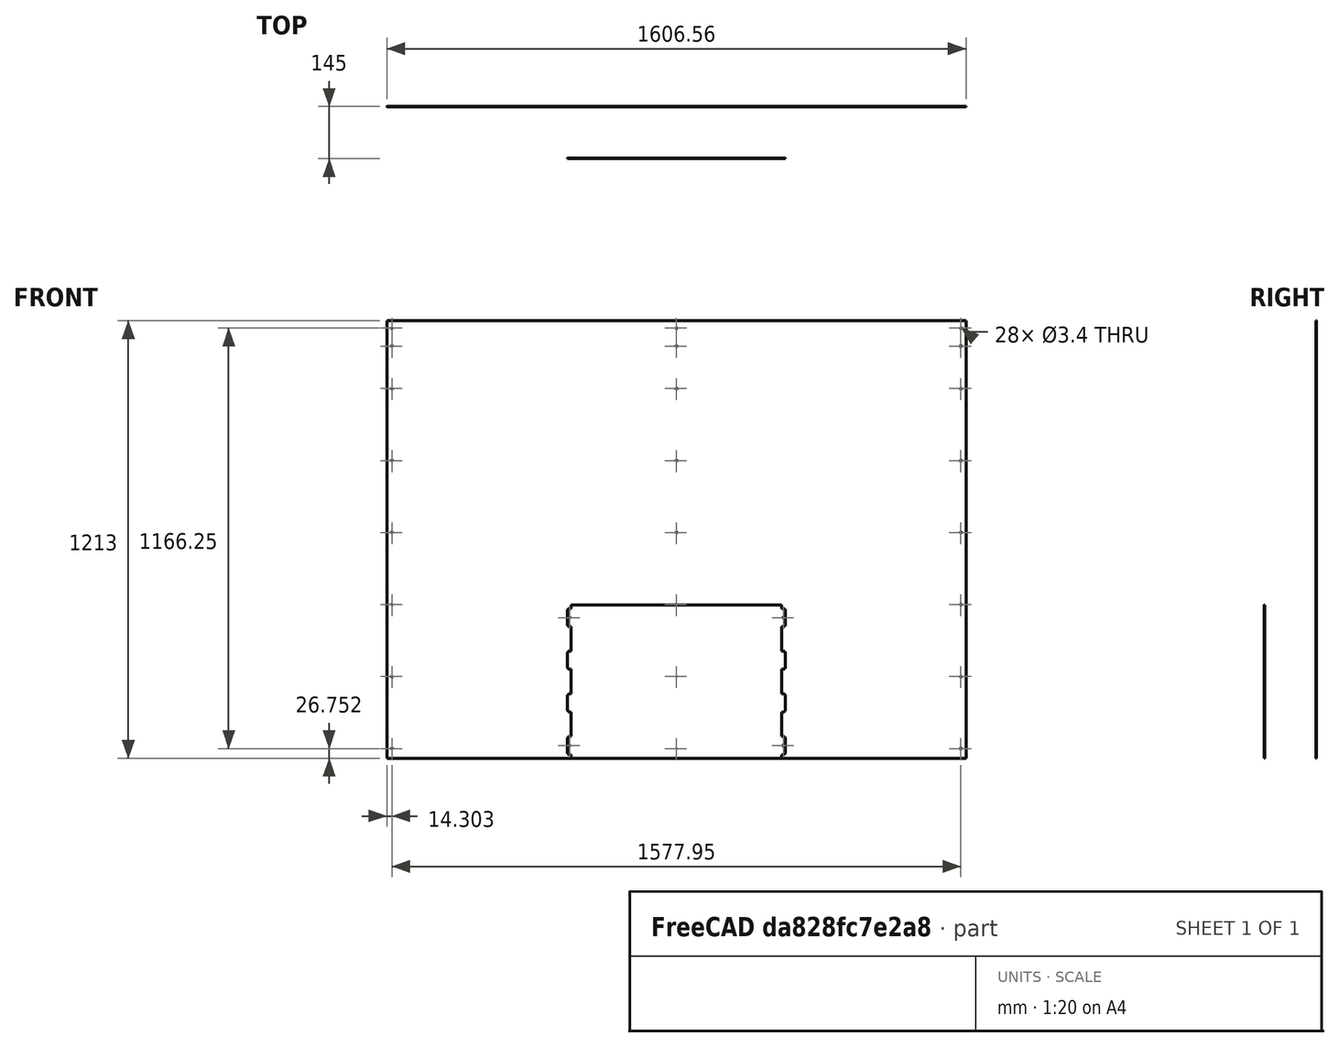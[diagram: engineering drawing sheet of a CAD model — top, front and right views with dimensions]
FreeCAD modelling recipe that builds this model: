
FCSTD DOCUMENT  (FreeCAD 0.21R32532 (Git))
Label: composit_full_size2part_plexiglass_cut
License: All rights reserved
LicenseURL: http://en.wikipedia.org/wiki/All_rights_reserved
objects: Sketcher::SketchObject×8, App::Link×3, Part::Feature×2, Part::FeaturePython×2, Part::Part2DObjectPython×1
note: 11 computed .brp shape members not serialized (recipe doc carries the construction recipe); baked Part::Feature solids carry a one-line shape summary decoded from their .brp
EXTERNAL_REF file=composit_full_size2part.FCStd obj=plexiglasss_shield
EXTERNAL_REF file=composit_full_size2part.FCStd obj=Body048
EXTERNAL_REF file=composit_full_size2part.FCStd obj=Body057

FEATURE [App::Link] Link
  LinkedObject = -> <external composit_full_size2part.FCStd>#plexiglasss_shield
  expr: LinkedObject = composit_full_size2part#plexiglasss_shield._self
FEATURE [App::Link] Link001
  LinkedObject = -> <external composit_full_size2part.FCStd>#Body048
  expr: LinkedObject = composit_full_size2part#<<plexiglass_shield_material_0.30ansi>>._self
FEATURE [Part::Feature] Unfold
  shape: bbox 1607 x 1 x 1213 mm, 30 faces (baked)
FEATURE [Sketcher::SketchObject] Unfold_Sketch
  FullyConstrained = false
  sketch-geometry (28):
    g0: LineSegment StartX=-803.277 StartY=0 StartZ=0 EndX=-803.277 EndY=-1213 EndZ=0
    g1: LineSegment StartX=803.277 StartY=0 StartZ=0 EndX=803.277 EndY=-1213 EndZ=0
    g2: Circle CenterX=788.977 CenterY=-1193 CenterZ=0 NormalX=0 NormalY=0 NormalZ=-1 AngleXU=-3.14159 Radius=1.7
    g3: Circle CenterX=788.977 CenterY=-1143.07 CenterZ=0 NormalX=0 NormalY=0 NormalZ=-1 AngleXU=-3.14159 Radius=1.7
    g4: Circle CenterX=788.977 CenterY=-1025.25 CenterZ=0 NormalX=0 NormalY=0 NormalZ=-1 AngleXU=-3.14159 Radius=1.7
    g5: Circle CenterX=-788.977 CenterY=-625.852 CenterZ=0 NormalX=0 NormalY=0 NormalZ=-1 AngleXU=-3.14159 Radius=1.7
    g6: Circle CenterX=-788.977 CenterY=-825.552 CenterZ=0 NormalX=0 NormalY=0 NormalZ=-1 AngleXU=-3.14159 Radius=1.7
    g7: Circle CenterX=-788.977 CenterY=-1025.25 CenterZ=0 NormalX=0 NormalY=0 NormalZ=-1 AngleXU=-3.14159 Radius=1.7
    g8: Circle CenterX=-788.977 CenterY=-1143.07 CenterZ=0 NormalX=0 NormalY=0 NormalZ=-1 AngleXU=-3.14159 Radius=1.7
    g9: Circle CenterX=-788.977 CenterY=-1193 CenterZ=0 NormalX=0 NormalY=0 NormalZ=-1 AngleXU=-3.14159 Radius=1.7
    g10: Circle CenterX=788.977 CenterY=-825.552 CenterZ=0 NormalX=0 NormalY=0 NormalZ=-1 AngleXU=-3.14159 Radius=1.7
    g11: Circle CenterX=788.977 CenterY=-625.852 CenterZ=0 NormalX=0 NormalY=0 NormalZ=-1 AngleXU=-3.14159 Radius=1.7
    g12: Circle CenterX=-7.45e-13 CenterY=-625.852 CenterZ=0 NormalX=0 NormalY=0 NormalZ=-1 AngleXU=-3.14159 Radius=1.7
    g13: Circle CenterX=-7.45e-13 CenterY=-1193 CenterZ=0 NormalX=0 NormalY=0 NormalZ=-1 AngleXU=-3.14159 Radius=1.7
    g14: Circle CenterX=-7.45e-13 CenterY=-1143.07 CenterZ=0 NormalX=0 NormalY=0 NormalZ=-1 AngleXU=-3.14159 Radius=1.7
    g15: Circle CenterX=-7.45e-13 CenterY=-1025.25 CenterZ=0 NormalX=0 NormalY=0 NormalZ=-1 AngleXU=-3.14159 Radius=1.7
    g16: Circle CenterX=-7.45e-13 CenterY=-825.552 CenterZ=0 NormalX=0 NormalY=0 NormalZ=-1 AngleXU=-3.14159 Radius=1.7
    g17: Circle CenterX=788.977 CenterY=-26.752 CenterZ=0 NormalX=0 NormalY=0 NormalZ=-1 AngleXU=-3.14159 Radius=1.7
    g18: Circle CenterX=-788.977 CenterY=-26.752 CenterZ=0 NormalX=0 NormalY=0 NormalZ=-1 AngleXU=-3.14159 Radius=1.7
    g19: Circle CenterX=788.977 CenterY=-226.452 CenterZ=0 NormalX=0 NormalY=0 NormalZ=-1 AngleXU=-3.14159 Radius=1.7
    g20: Circle CenterX=788.977 CenterY=-426.152 CenterZ=0 NormalX=0 NormalY=0 NormalZ=-1 AngleXU=-3.14159 Radius=1.7
    g21: Circle CenterX=-788.977 CenterY=-426.152 CenterZ=0 NormalX=0 NormalY=0 NormalZ=-1 AngleXU=-3.14159 Radius=1.7
    g22: Circle CenterX=-788.977 CenterY=-226.452 CenterZ=0 NormalX=0 NormalY=0 NormalZ=-1 AngleXU=-3.14159 Radius=1.7
    g23: Circle CenterX=-7.45e-13 CenterY=-26.752 CenterZ=0 NormalX=0 NormalY=0 NormalZ=-1 AngleXU=-3.14159 Radius=1.7
    g24: Circle CenterX=-7.45e-13 CenterY=-426.152 CenterZ=0 NormalX=0 NormalY=0 NormalZ=-1 AngleXU=-3.14159 Radius=1.7
    g25: Circle CenterX=-7.45e-13 CenterY=-226.452 CenterZ=0 NormalX=0 NormalY=0 NormalZ=-1 AngleXU=-3.14159 Radius=1.7
    g26: LineSegment StartX=-803.277 StartY=-1213 StartZ=0 EndX=803.277 EndY=-1213 EndZ=0
    g27: LineSegment StartX=803.277 StartY=0 StartZ=0 EndX=-803.277 EndY=0 EndZ=0
FEATURE [Sketcher::SketchObject] Unfold_Sketch_Outline
  FullyConstrained = false
  sketch-geometry (4):
    g0: LineSegment StartX=803.277 StartY=0 StartZ=0 EndX=-803.277 EndY=0 EndZ=0
    g1: LineSegment StartX=-803.277 StartY=0 StartZ=0 EndX=-803.277 EndY=-1213 EndZ=0
    g2: LineSegment StartX=-803.277 StartY=-1213 StartZ=0 EndX=803.277 EndY=-1213 EndZ=0
    g3: LineSegment StartX=803.277 StartY=0 StartZ=0 EndX=803.277 EndY=-1213 EndZ=0
FEATURE [Sketcher::SketchObject] Unfold_Sketch_Internal
  FullyConstrained = false
  sketch-geometry (24):
    g0: Circle CenterX=-7.45e-13 CenterY=-226.452 CenterZ=0 NormalX=0 NormalY=0 NormalZ=-1 AngleXU=-3.14159 Radius=1.7
    g1: Circle CenterX=-7.45e-13 CenterY=-426.152 CenterZ=0 NormalX=0 NormalY=0 NormalZ=-1 AngleXU=-3.14159 Radius=1.7
    g2: Circle CenterX=-7.45e-13 CenterY=-825.552 CenterZ=0 NormalX=0 NormalY=0 NormalZ=-1 AngleXU=-3.14159 Radius=1.7
    g3: Circle CenterX=-7.45e-13 CenterY=-1025.25 CenterZ=0 NormalX=0 NormalY=0 NormalZ=-1 AngleXU=-3.14159 Radius=1.7
    g4: Circle CenterX=-7.45e-13 CenterY=-1143.07 CenterZ=0 NormalX=0 NormalY=0 NormalZ=-1 AngleXU=-3.14159 Radius=1.7
    g5: Circle CenterX=-7.45e-13 CenterY=-1193 CenterZ=0 NormalX=0 NormalY=0 NormalZ=-1 AngleXU=-3.14159 Radius=1.7
    g6: Circle CenterX=-7.45e-13 CenterY=-625.852 CenterZ=0 NormalX=0 NormalY=0 NormalZ=-1 AngleXU=-3.14159 Radius=1.7
    g7: Circle CenterX=-7.45e-13 CenterY=-26.752 CenterZ=0 NormalX=0 NormalY=0 NormalZ=-1 AngleXU=-3.14159 Radius=1.7
    g8: Circle CenterX=-788.977 CenterY=-226.452 CenterZ=0 NormalX=0 NormalY=0 NormalZ=-1 AngleXU=-3.14159 Radius=1.7
    g9: Circle CenterX=-788.977 CenterY=-426.152 CenterZ=0 NormalX=0 NormalY=0 NormalZ=-1 AngleXU=-3.14159 Radius=1.7
    g10: Circle CenterX=788.977 CenterY=-426.152 CenterZ=0 NormalX=0 NormalY=0 NormalZ=-1 AngleXU=-3.14159 Radius=1.7
    g11: Circle CenterX=788.977 CenterY=-226.452 CenterZ=0 NormalX=0 NormalY=0 NormalZ=-1 AngleXU=-3.14159 Radius=1.7
    g12: Circle CenterX=788.977 CenterY=-625.852 CenterZ=0 NormalX=0 NormalY=0 NormalZ=-1 AngleXU=-3.14159 Radius=1.7
    g13: Circle CenterX=788.977 CenterY=-825.552 CenterZ=0 NormalX=0 NormalY=0 NormalZ=-1 AngleXU=-3.14159 Radius=1.7
    g14: Circle CenterX=-788.977 CenterY=-1193 CenterZ=0 NormalX=0 NormalY=0 NormalZ=-1 AngleXU=-3.14159 Radius=1.7
    g15: Circle CenterX=-788.977 CenterY=-1143.07 CenterZ=0 NormalX=0 NormalY=0 NormalZ=-1 AngleXU=-3.14159 Radius=1.7
    g16: Circle CenterX=-788.977 CenterY=-1025.25 CenterZ=0 NormalX=0 NormalY=0 NormalZ=-1 AngleXU=-3.14159 Radius=1.7
    g17: Circle CenterX=-788.977 CenterY=-825.552 CenterZ=0 NormalX=0 NormalY=0 NormalZ=-1 AngleXU=-3.14159 Radius=1.7
    g18: Circle CenterX=-788.977 CenterY=-625.852 CenterZ=0 NormalX=0 NormalY=0 NormalZ=-1 AngleXU=-3.14159 Radius=1.7
    g19: Circle CenterX=788.977 CenterY=-1025.25 CenterZ=0 NormalX=0 NormalY=0 NormalZ=-1 AngleXU=-3.14159 Radius=1.7
    g20: Circle CenterX=788.977 CenterY=-1143.07 CenterZ=0 NormalX=0 NormalY=0 NormalZ=-1 AngleXU=-3.14159 Radius=1.7
    g21: Circle CenterX=788.977 CenterY=-1193 CenterZ=0 NormalX=0 NormalY=0 NormalZ=-1 AngleXU=-3.14159 Radius=1.7
    g22: Circle CenterX=-788.977 CenterY=-26.752 CenterZ=0 NormalX=0 NormalY=0 NormalZ=-1 AngleXU=-3.14159 Radius=1.7
    g23: Circle CenterX=788.977 CenterY=-26.752 CenterZ=0 NormalX=0 NormalY=0 NormalZ=-1 AngleXU=-3.14159 Radius=1.7
FEATURE [Sketcher::SketchObject] Unfold_Sketch_bends
  FullyConstrained = false
  sketch-geometry (6):
    g0: LineSegment StartX=-678.962 StartY=-1213 StartZ=0 EndX=-678.962 EndY=0 EndZ=0
    g1: LineSegment StartX=-394.489 StartY=-1213 StartZ=0 EndX=-394.489 EndY=0 EndZ=0
    g2: LineSegment StartX=-110.015 StartY=-1213 StartZ=0 EndX=-110.015 EndY=0 EndZ=0
    g3: LineSegment StartX=678.962 StartY=-1213 StartZ=0 EndX=678.962 EndY=0 EndZ=0
    g4: LineSegment StartX=394.489 StartY=-1213 StartZ=0 EndX=394.489 EndY=0 EndZ=0
    g5: LineSegment StartX=110.015 StartY=-1213 StartZ=0 EndX=110.015 EndY=0 EndZ=0
FEATURE [Part::Feature] Unfold001
  shape: bbox 603.8 x 1.5 x 425 mm, 58 faces (baked)
FEATURE [Sketcher::SketchObject] Unfold_Sketch001
  FullyConstrained = false
  sketch-geometry (56):
    g0: LineSegment StartX=0 StartY=291.917 StartZ=0 EndX=-10 EndY=291.917 EndZ=0
    g1: LineSegment StartX=-10 StartY=291.917 StartZ=0 EndX=-10 EndY=296.917 EndZ=0
    g2: ArcOfCircle CenterX=-15 CenterY=296.917 CenterZ=0 NormalX=0 NormalY=0 NormalZ=1 AngleXU=1.5708 Radius=5 StartAngle=4.71239 EndAngle=6.28319
    g3: LineSegment StartX=-15 StartY=301.917 StartZ=0 EndX=-55 EndY=301.917 EndZ=0
    g4: ArcOfCircle CenterX=-55 CenterY=296.917 CenterZ=0 NormalX=0 NormalY=0 NormalZ=1 AngleXU=1.5708 Radius=5 StartAngle=0 EndAngle=1.5708
    g5: LineSegment StartX=-60 StartY=296.917 StartZ=0 EndX=-60 EndY=291.917 EndZ=0
    g6: LineSegment StartX=-60 StartY=291.917 StartZ=0 EndX=-128.333 EndY=291.917 EndZ=0
    g7: LineSegment StartX=-128.333 StartY=291.917 StartZ=0 EndX=-128.333 EndY=296.917 EndZ=0
    g8: ArcOfCircle CenterX=-133.333 CenterY=296.917 CenterZ=0 NormalX=0 NormalY=0 NormalZ=1 AngleXU=1.5708 Radius=5 StartAngle=4.71239 EndAngle=6.28319
    g9: LineSegment StartX=-133.333 StartY=301.917 StartZ=0 EndX=-173.333 EndY=301.917 EndZ=0
    g10: ArcOfCircle CenterX=-173.333 CenterY=296.917 CenterZ=0 NormalX=0 NormalY=0 NormalZ=1 AngleXU=1.5708 Radius=5 StartAngle=2e-15 EndAngle=1.5708
    g11: LineSegment StartX=-178.333 StartY=296.917 StartZ=0 EndX=-178.333 EndY=291.917 EndZ=0
    g12: LineSegment StartX=-178.333 StartY=291.917 StartZ=0 EndX=-246.667 EndY=291.917 EndZ=0
    g13: LineSegment StartX=-246.667 StartY=291.917 StartZ=0 EndX=-246.667 EndY=296.917 EndZ=0
    g14: ArcOfCircle CenterX=-251.667 CenterY=296.917 CenterZ=0 NormalX=0 NormalY=0 NormalZ=1 AngleXU=1.5708 Radius=5 StartAngle=4.71239 EndAngle=6.28319
    g15: LineSegment StartX=-251.667 StartY=301.917 StartZ=0 EndX=-291.667 EndY=301.917 EndZ=0
    g16: ArcOfCircle CenterX=-291.667 CenterY=296.917 CenterZ=0 NormalX=0 NormalY=0 NormalZ=1 AngleXU=1.5708 Radius=5 StartAngle=0 EndAngle=1.5708
    g17: LineSegment StartX=-296.667 StartY=296.917 StartZ=0 EndX=-296.667 EndY=291.917 EndZ=0
    g18: LineSegment StartX=-296.667 StartY=291.917 StartZ=0 EndX=-365 EndY=291.917 EndZ=0
    g19: LineSegment StartX=-365 StartY=291.917 StartZ=0 EndX=-365 EndY=296.917 EndZ=0
    g20: ArcOfCircle CenterX=-370 CenterY=296.917 CenterZ=0 NormalX=0 NormalY=0 NormalZ=1 AngleXU=1.5708 Radius=5 StartAngle=4.71239 EndAngle=6.28319
    g21: LineSegment StartX=-370 StartY=301.917 StartZ=0 EndX=-410 EndY=301.917 EndZ=0
    g22: ArcOfCircle CenterX=-410 CenterY=296.917 CenterZ=0 NormalX=0 NormalY=0 NormalZ=1 AngleXU=1.5708 Radius=5 StartAngle=0 EndAngle=1.5708
    g23: LineSegment StartX=-415 StartY=296.917 StartZ=0 EndX=-415 EndY=291.917 EndZ=0
    g24: LineSegment StartX=-415 StartY=291.917 StartZ=0 EndX=-425 EndY=291.917 EndZ=0
    g25: LineSegment StartX=0 StartY=291.917 StartZ=0 EndX=0 EndY=-291.917 EndZ=0
    g26: LineSegment StartX=-425 StartY=-291.917 StartZ=0 EndX=-425 EndY=291.917 EndZ=0
    g27: LineSegment StartX=-415 StartY=-291.917 StartZ=0 EndX=-425 EndY=-291.917 EndZ=0
    g28: LineSegment StartX=-415 StartY=-296.917 StartZ=0 EndX=-415 EndY=-291.917 EndZ=0
    g29: ArcOfCircle CenterX=-410 CenterY=-296.917 CenterZ=0 NormalX=0 NormalY=0 NormalZ=1 AngleXU=-1.5708 Radius=5 StartAngle=4.71239 EndAngle=6.28319
    g30: LineSegment StartX=-370 StartY=-301.917 StartZ=0 EndX=-410 EndY=-301.917 EndZ=0
    g31: ArcOfCircle CenterX=-370 CenterY=-296.917 CenterZ=0 NormalX=0 NormalY=0 NormalZ=1 AngleXU=-1.5708 Radius=5 StartAngle=2.7e-15 EndAngle=1.5708
    g32: LineSegment StartX=-365 StartY=-291.917 StartZ=0 EndX=-365 EndY=-296.917 EndZ=0
    g33: LineSegment StartX=-296.667 StartY=-291.917 StartZ=0 EndX=-365 EndY=-291.917 EndZ=0
    g34: LineSegment StartX=-296.667 StartY=-296.917 StartZ=0 EndX=-296.667 EndY=-291.917 EndZ=0
    g35: ArcOfCircle CenterX=-291.667 CenterY=-296.917 CenterZ=0 NormalX=0 NormalY=0 NormalZ=1 AngleXU=-1.5708 Radius=5 StartAngle=4.71239 EndAngle=6.28319
    g36: LineSegment StartX=-251.667 StartY=-301.917 StartZ=0 EndX=-291.667 EndY=-301.917 EndZ=0
    g37: ArcOfCircle CenterX=-251.667 CenterY=-296.917 CenterZ=0 NormalX=0 NormalY=0 NormalZ=1 AngleXU=-1.5708 Radius=5 StartAngle=2.7e-15 EndAngle=1.5708
    g38: LineSegment StartX=-246.667 StartY=-291.917 StartZ=0 EndX=-246.667 EndY=-296.917 EndZ=0
    g39: LineSegment StartX=-178.333 StartY=-291.917 StartZ=0 EndX=-246.667 EndY=-291.917 EndZ=0
    g40: LineSegment StartX=-178.333 StartY=-296.917 StartZ=0 EndX=-178.333 EndY=-291.917 EndZ=0
    g41: ArcOfCircle CenterX=-173.333 CenterY=-296.917 CenterZ=0 NormalX=0 NormalY=0 NormalZ=1 AngleXU=-1.5708 Radius=5 StartAngle=4.71239 EndAngle=6.28319
    g42: LineSegment StartX=-133.333 StartY=-301.917 StartZ=0 EndX=-173.333 EndY=-301.917 EndZ=0
    g43: ArcOfCircle CenterX=-133.333 CenterY=-296.917 CenterZ=0 NormalX=0 NormalY=0 NormalZ=1 AngleXU=-1.5708 Radius=5 StartAngle=0 EndAngle=1.5708
    g44: LineSegment StartX=-128.333 StartY=-291.917 StartZ=0 EndX=-128.333 EndY=-296.917 EndZ=0
    g45: LineSegment StartX=-60 StartY=-291.917 StartZ=0 EndX=-128.333 EndY=-291.917 EndZ=0
    g46: LineSegment StartX=-60 StartY=-296.917 StartZ=0 EndX=-60 EndY=-291.917 EndZ=0
    g47: ArcOfCircle CenterX=-55 CenterY=-296.917 CenterZ=0 NormalX=0 NormalY=0 NormalZ=1 AngleXU=-1.5708 Radius=5 StartAngle=4.71239 EndAngle=6.28319
    g48: LineSegment StartX=-15 StartY=-301.917 StartZ=0 EndX=-55 EndY=-301.917 EndZ=0
    g49: ArcOfCircle CenterX=-15 CenterY=-296.917 CenterZ=0 NormalX=0 NormalY=0 NormalZ=1 AngleXU=-1.5708 Radius=5 StartAngle=0 EndAngle=1.5708
    g50: LineSegment StartX=-10 StartY=-291.917 StartZ=0 EndX=-10 EndY=-296.917 EndZ=0
    g51: LineSegment StartX=0 StartY=-291.917 StartZ=0 EndX=-10 EndY=-291.917 EndZ=0
    g52: Circle CenterX=-35 CenterY=-296.417 CenterZ=0 NormalX=0 NormalY=0 NormalZ=-1 AngleXU=-1.5708 Radius=1.7
    g53: Circle CenterX=-35 CenterY=296.417 CenterZ=0 NormalX=0 NormalY=0 NormalZ=1 AngleXU=1.5708 Radius=1.7
    g54: Circle CenterX=-390 CenterY=-296.417 CenterZ=0 NormalX=0 NormalY=0 NormalZ=-1 AngleXU=-1.5708 Radius=1.7
    g55: Circle CenterX=-390 CenterY=296.417 CenterZ=0 NormalX=0 NormalY=0 NormalZ=1 AngleXU=1.5708 Radius=1.7
FEATURE [Sketcher::SketchObject] Unfold_Sketch_Outline001
  FullyConstrained = false
  Placement = pos=(302,425,0) rot=(0,0,1;1.5708rad)
  sketch-geometry (52):
    g0: LineSegment StartX=0 StartY=291.917 StartZ=0 EndX=-10 EndY=291.917 EndZ=0
    g1: LineSegment StartX=-10 StartY=291.917 StartZ=0 EndX=-10 EndY=296.917 EndZ=0
    g2: ArcOfCircle CenterX=-15 CenterY=296.917 CenterZ=0 NormalX=0 NormalY=0 NormalZ=1 AngleXU=1.5708 Radius=5 StartAngle=4.71239 EndAngle=6.28319
    g3: LineSegment StartX=-15 StartY=301.917 StartZ=0 EndX=-55 EndY=301.917 EndZ=0
    g4: ArcOfCircle CenterX=-55 CenterY=296.917 CenterZ=0 NormalX=0 NormalY=0 NormalZ=1 AngleXU=1.5708 Radius=5 StartAngle=0 EndAngle=1.5708
    g5: LineSegment StartX=-60 StartY=296.917 StartZ=0 EndX=-60 EndY=291.917 EndZ=0
    g6: LineSegment StartX=-60 StartY=291.917 StartZ=0 EndX=-128.333 EndY=291.917 EndZ=0
    g7: LineSegment StartX=-128.333 StartY=291.917 StartZ=0 EndX=-128.333 EndY=296.917 EndZ=0
    g8: ArcOfCircle CenterX=-133.333 CenterY=296.917 CenterZ=0 NormalX=0 NormalY=0 NormalZ=1 AngleXU=1.5708 Radius=5 StartAngle=4.71239 EndAngle=6.28319
    g9: LineSegment StartX=-133.333 StartY=301.917 StartZ=0 EndX=-173.333 EndY=301.917 EndZ=0
    g10: ArcOfCircle CenterX=-173.333 CenterY=296.917 CenterZ=0 NormalX=0 NormalY=0 NormalZ=1 AngleXU=1.5708 Radius=5 StartAngle=2e-15 EndAngle=1.5708
    g11: LineSegment StartX=-178.333 StartY=296.917 StartZ=0 EndX=-178.333 EndY=291.917 EndZ=0
    g12: LineSegment StartX=-178.333 StartY=291.917 StartZ=0 EndX=-246.667 EndY=291.917 EndZ=0
    g13: LineSegment StartX=-246.667 StartY=291.917 StartZ=0 EndX=-246.667 EndY=296.917 EndZ=0
    g14: ArcOfCircle CenterX=-251.667 CenterY=296.917 CenterZ=0 NormalX=0 NormalY=0 NormalZ=1 AngleXU=1.5708 Radius=5 StartAngle=4.71239 EndAngle=6.28319
    g15: LineSegment StartX=-251.667 StartY=301.917 StartZ=0 EndX=-291.667 EndY=301.917 EndZ=0
    g16: ArcOfCircle CenterX=-291.667 CenterY=296.917 CenterZ=0 NormalX=0 NormalY=0 NormalZ=1 AngleXU=1.5708 Radius=5 StartAngle=0 EndAngle=1.5708
    g17: LineSegment StartX=-296.667 StartY=296.917 StartZ=0 EndX=-296.667 EndY=291.917 EndZ=0
    g18: LineSegment StartX=-296.667 StartY=291.917 StartZ=0 EndX=-365 EndY=291.917 EndZ=0
    g19: LineSegment StartX=-365 StartY=291.917 StartZ=0 EndX=-365 EndY=296.917 EndZ=0
    g20: ArcOfCircle CenterX=-370 CenterY=296.917 CenterZ=0 NormalX=0 NormalY=0 NormalZ=1 AngleXU=1.5708 Radius=5 StartAngle=4.71239 EndAngle=6.28319
    g21: LineSegment StartX=-370 StartY=301.917 StartZ=0 EndX=-410 EndY=301.917 EndZ=0
    g22: ArcOfCircle CenterX=-410 CenterY=296.917 CenterZ=0 NormalX=0 NormalY=0 NormalZ=1 AngleXU=1.5708 Radius=5 StartAngle=0 EndAngle=1.5708
    g23: LineSegment StartX=-415 StartY=296.917 StartZ=0 EndX=-415 EndY=291.917 EndZ=0
    g24: LineSegment StartX=-415 StartY=291.917 StartZ=0 EndX=-425 EndY=291.917 EndZ=0
    g25: LineSegment StartX=-425 StartY=-291.917 StartZ=0 EndX=-425 EndY=291.917 EndZ=0
    g26: LineSegment StartX=-415 StartY=-291.917 StartZ=0 EndX=-425 EndY=-291.917 EndZ=0
    g27: LineSegment StartX=-415 StartY=-296.917 StartZ=0 EndX=-415 EndY=-291.917 EndZ=0
    g28: ArcOfCircle CenterX=-410 CenterY=-296.917 CenterZ=0 NormalX=0 NormalY=0 NormalZ=1 AngleXU=-1.5708 Radius=5 StartAngle=4.71239 EndAngle=6.28319
    g29: LineSegment StartX=-370 StartY=-301.917 StartZ=0 EndX=-410 EndY=-301.917 EndZ=0
    g30: ArcOfCircle CenterX=-370 CenterY=-296.917 CenterZ=0 NormalX=0 NormalY=0 NormalZ=1 AngleXU=-1.5708 Radius=5 StartAngle=2.7e-15 EndAngle=1.5708
    g31: LineSegment StartX=-365 StartY=-291.917 StartZ=0 EndX=-365 EndY=-296.917 EndZ=0
    g32: LineSegment StartX=-296.667 StartY=-291.917 StartZ=0 EndX=-365 EndY=-291.917 EndZ=0
    g33: LineSegment StartX=-296.667 StartY=-296.917 StartZ=0 EndX=-296.667 EndY=-291.917 EndZ=0
    g34: ArcOfCircle CenterX=-291.667 CenterY=-296.917 CenterZ=0 NormalX=0 NormalY=0 NormalZ=1 AngleXU=-1.5708 Radius=5 StartAngle=4.71239 EndAngle=6.28319
    g35: LineSegment StartX=-251.667 StartY=-301.917 StartZ=0 EndX=-291.667 EndY=-301.917 EndZ=0
    g36: ArcOfCircle CenterX=-251.667 CenterY=-296.917 CenterZ=0 NormalX=0 NormalY=0 NormalZ=1 AngleXU=-1.5708 Radius=5 StartAngle=2.7e-15 EndAngle=1.5708
    g37: LineSegment StartX=-246.667 StartY=-291.917 StartZ=0 EndX=-246.667 EndY=-296.917 EndZ=0
    g38: LineSegment StartX=-178.333 StartY=-291.917 StartZ=0 EndX=-246.667 EndY=-291.917 EndZ=0
    g39: LineSegment StartX=-178.333 StartY=-296.917 StartZ=0 EndX=-178.333 EndY=-291.917 EndZ=0
    g40: ArcOfCircle CenterX=-173.333 CenterY=-296.917 CenterZ=0 NormalX=0 NormalY=0 NormalZ=1 AngleXU=-1.5708 Radius=5 StartAngle=4.71239 EndAngle=6.28319
    g41: LineSegment StartX=-133.333 StartY=-301.917 StartZ=0 EndX=-173.333 EndY=-301.917 EndZ=0
    g42: ArcOfCircle CenterX=-133.333 CenterY=-296.917 CenterZ=0 NormalX=0 NormalY=0 NormalZ=1 AngleXU=-1.5708 Radius=5 StartAngle=0 EndAngle=1.5708
    g43: LineSegment StartX=-128.333 StartY=-291.917 StartZ=0 EndX=-128.333 EndY=-296.917 EndZ=0
    g44: LineSegment StartX=-60 StartY=-291.917 StartZ=0 EndX=-128.333 EndY=-291.917 EndZ=0
    g45: LineSegment StartX=-60 StartY=-296.917 StartZ=0 EndX=-60 EndY=-291.917 EndZ=0
    g46: ArcOfCircle CenterX=-55 CenterY=-296.917 CenterZ=0 NormalX=0 NormalY=0 NormalZ=1 AngleXU=-1.5708 Radius=5 StartAngle=4.71239 EndAngle=6.28319
    g47: LineSegment StartX=-15 StartY=-301.917 StartZ=0 EndX=-55 EndY=-301.917 EndZ=0
    g48: ArcOfCircle CenterX=-15 CenterY=-296.917 CenterZ=0 NormalX=0 NormalY=0 NormalZ=1 AngleXU=-1.5708 Radius=5 StartAngle=0 EndAngle=1.5708
    g49: LineSegment StartX=-10 StartY=-291.917 StartZ=0 EndX=-10 EndY=-296.917 EndZ=0
    g50: LineSegment StartX=0 StartY=-291.917 StartZ=0 EndX=-10 EndY=-291.917 EndZ=0
    g51: LineSegment StartX=0 StartY=291.917 StartZ=0 EndX=0 EndY=-291.917 EndZ=0
FEATURE [Sketcher::SketchObject] Unfold_Sketch_Internal001
  FullyConstrained = false
  sketch-geometry (4):
    g0: Circle CenterX=-390 CenterY=296.417 CenterZ=0 NormalX=0 NormalY=0 NormalZ=1 AngleXU=1.5708 Radius=1.7
    g1: Circle CenterX=-390 CenterY=-296.417 CenterZ=0 NormalX=0 NormalY=0 NormalZ=-1 AngleXU=-1.5708 Radius=1.7
    g2: Circle CenterX=-35 CenterY=296.417 CenterZ=0 NormalX=0 NormalY=0 NormalZ=1 AngleXU=1.5708 Radius=1.7
    g3: Circle CenterX=-35 CenterY=-296.417 CenterZ=0 NormalX=0 NormalY=0 NormalZ=-1 AngleXU=-1.5708 Radius=1.7
FEATURE [Sketcher::SketchObject] Unfold_Sketch_bends001
  FullyConstrained = false
  sketch-geometry (2):
    g0: LineSegment StartX=-425 StartY=-135.958 StartZ=0 EndX=0 EndY=-135.958 EndZ=0
    g1: LineSegment StartX=-425 StartY=135.958 StartZ=0 EndX=0 EndY=135.958 EndZ=0
FEATURE [App::Link] Link002  label="plexiglass_top"
  LinkPlacement = pos=(96,345,0) rot=(0,0,1;1.5708rad)
  LinkedObject = -> <external composit_full_size2part.FCStd>#Body057
  Placement = pos=(96,345,0) rot=(0,0,1;1.5708rad)
FEATURE [Part::FeaturePython] Array  # Draft array (typed FeaturePython)
  AlwaysSyncPlacement = false
  Angle = 360
  ArrayType = 0
  Axis = (0,0,1)
  Base = -> Link002
  Center = (0,0,0)
  Count = 24
  ExpandArray = false
  Fuse = false
  IntervalAxis = (0,0,0)
  IntervalX = (100,0,0)
  IntervalY = (0,694,0)
  IntervalZ = (0,0,100)
  NumberCircles = 3
  NumberPolar = 5
  NumberX = 12
  NumberY = 2
  NumberZ = 1
  PlacementList = 24 placements: [(96,345,0),(96,1039,0),(196,345,0),(196,1039,0),(296,345,0),(296,1039,0),(396,345,0),(396,1039,0),(496,345,0),(496,1039,0),(596,345,0),(596,1039,0),(696,345,0),(696,1039,0),(796,345,0),(796,1039,0),(896,345,0),(896,1039,0),(996,345,0),(996,1039,0),(1096,345,0),(1096,1039,0),(1196,345,0),(1196,1039,0)]
  RadialDistance = 50
  ScaleList = (24) [(1,1,1),(1,1,1),(1,1,1),(1,1,1),(1,1,1),(1,1,1),(1,1,1),(1,1,1),(1,1,1),(1,1,1),(1,1,1),(1,1,1),(1,1,1),(1,1,1),(1,1,1),(1,1,1),(1,1,1),(1,1,1),+6 more]
  Symmetry = 1
  TangentialDistance = 25
FEATURE [Part::Part2DObjectPython] Rectangle  # Draft 2D object (typed FeaturePython)
  Area = 2562500
  ChamferSize = 0
  Columns = 1
  FilletRadius = 0
  Height = 2050
  Length = 1250
  MakeFace = true
  Rows = 1
FEATURE [Part::FeaturePython] Array001  # Draft array (typed FeaturePython)
  AlwaysSyncPlacement = false
  Angle = 360
  ArrayType = 0
  Axis = (0,0,1)
  Base = -> Unfold_Sketch_Outline001
  Center = (0,0,0)
  Count = 8
  ExpandArray = false
  Fuse = false
  IntervalAxis = (0,0,0)
  IntervalX = (613,0,0)
  IntervalY = (0,430,0)
  IntervalZ = (0,0,100)
  NumberCircles = 3
  NumberPolar = 5
  NumberX = 2
  NumberY = 4
  NumberZ = 1
  PlacementList = 8 placements: [(302,425,0),(302,855,0),(302,1285,0),(302,1715,0),(915,425,0),(915,855,0),(915,1285,0),(915,1715,0)]
  RadialDistance = 50
  ScaleList = (8) [(1,1,1),(1,1,1),(1,1,1),(1,1,1),(1,1,1),(1,1,1),(1,1,1),(1,1,1)]
  Symmetry = 1
  TangentialDistance = 25
